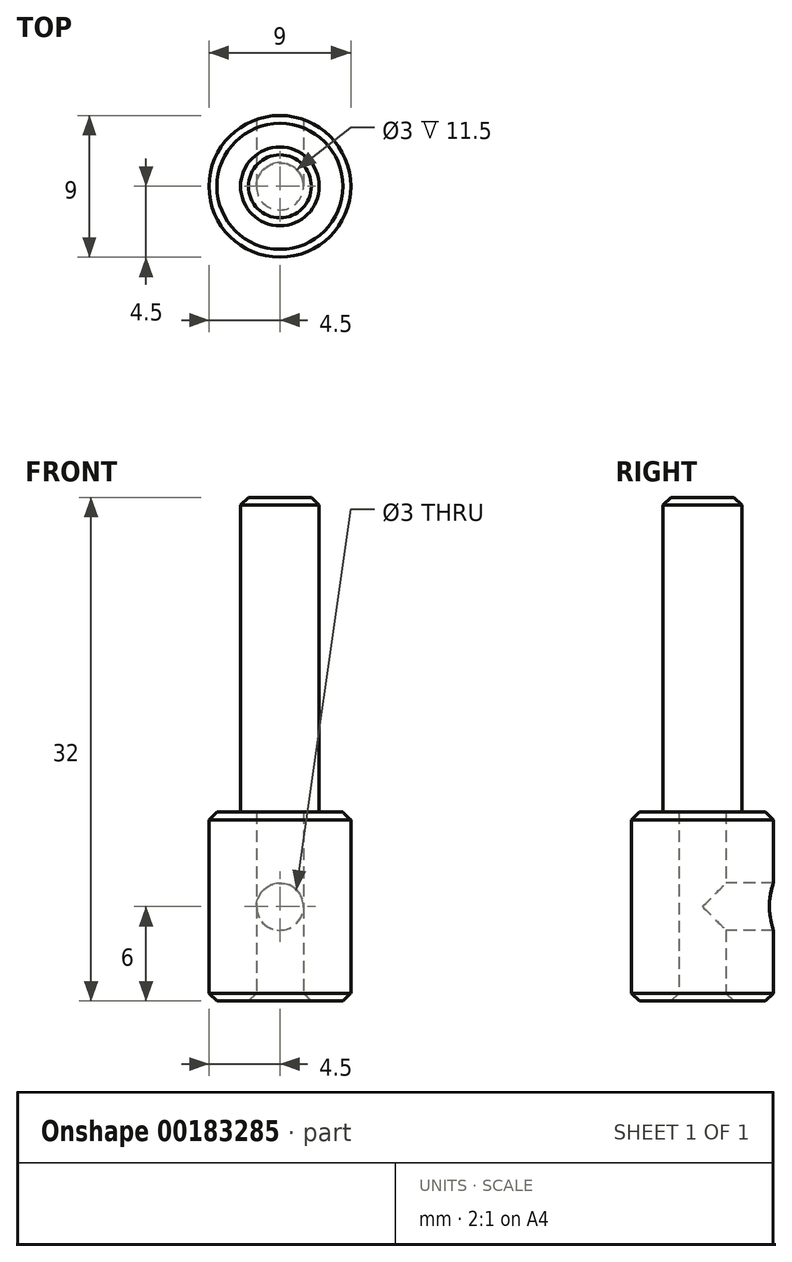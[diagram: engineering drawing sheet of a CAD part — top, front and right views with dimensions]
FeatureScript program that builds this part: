
annotation { "Feature Type Name" : "Feature", "Feature Type Description" : "" }
export const myFeature = defineFeature(function(context is Context, id is Id, definition is map)
    precondition{}
    {
        {
            var Q0;
            Q0=qCreatedBy(makeId("Top.planeOp"),FACE);
            var sketch = newSketch(context, id + "F0", { "sketchPlane" : qUnion([Q0])});
            skCircle(sketch, "E0", {"center": v(0, 0) * mm, "radius": 1.5 * mm});
            skCircle(sketch, "E1", {"center": v(0, 0) * mm, "radius": 4.5 * mm});
            skSolve(sketch);
        }
        {
            var Q0;
            Q0 = qSketchRegion(id + "F0", true);
            var Q1;
            Q1 = qConstructionFilter(qBodyType(qCreatedBy(id + "F0" ,EDGE), BodyType.WIRE), ConstructionObject.NO);
            extrude(context, id + "F1", {"entities" : qUnion([Q0]), "surfaceEntities" : qUnion([Q1]), "endBound" : BoundingType.SYMMETRIC, "depth" : 12 * mm});
        }
        {
            var Q0;
            Q0=makeQuery(id+"F1.opExtrude","CAP_FACE",FACE,{"disambiguationData":[OSD([sQuery(id+"F0.wireOp",EDGE,"E0"),sQuery(id+"F0.wireOp",EDGE,"E1")])],"isStart":false});
            var sketch = newSketch(context, id + "F2", { "sketchPlane" : qUnion([Q0])});
            skCircle(sketch, "E2", {"center": v(0, 0) * mm, "radius": 2.5 * mm});
            skSolve(sketch);
        }
        {
            var Q0;
            Q0 = qSketchRegion(id + "F2", true);
            extrude(context, id + "F3", {"entities" : qUnion([Q0]), "operationType" : NewBodyOperationType.ADD, "depth" : 20 * mm});
        }
        {
            var Q0;
            Q0=makeQuery(id+"F3.opExtrude","CAP_EDGE",EDGE,{"disambiguationData":[OSD([sQuery(id+"F2.wireOp",EDGE,"E2")])],"isStart":false});
            var Q1;
            Q1=makeQuery(id+"F1.opExtrude","CAP_EDGE",EDGE,{"disambiguationData":[OSD([sQuery(id+"F0.wireOp",EDGE,"E1")])],"isStart":false});
            var Q2;
            Q2=makeQuery(id+"F1.opExtrude","CAP_EDGE",EDGE,{"disambiguationData":[OSD([sQuery(id+"F0.wireOp",EDGE,"E0")])],"isStart":true});
            var Q3;
            Q3=makeQuery(id+"F1.opExtrude","CAP_EDGE",EDGE,{"disambiguationData":[OSD([sQuery(id+"F0.wireOp",EDGE,"E1")])],"isStart":true});
            chamfer(context, id + "F4", {"entities" : qUnion([Q0, Q1, Q2, Q3]), "width" : 0.5 * mm, "tangentPropagation" : true});
        }
        {
            var Q0;
            Q0=qCreatedBy(makeId("Front.planeOp"),FACE);
            var sketch = newSketch(context, id + "F5", { "sketchPlane" : qUnion([Q0])});
            skCircle(sketch, "E3", {"center": v(0, 0) * mm, "radius": 1.5 * mm});
            skSolve(sketch);
        }
        {
            var Q0;
            Q0 = qSketchRegion(id + "F5", true);
            extrude(context, id + "F6", {"entities" : qUnion([Q0]), "operationType" : NewBodyOperationType.REMOVE, "endBound" : BoundingType.THROUGH_ALL, "oppositeDirection" : true, "depth" : 25 * mm});
        }
    });
